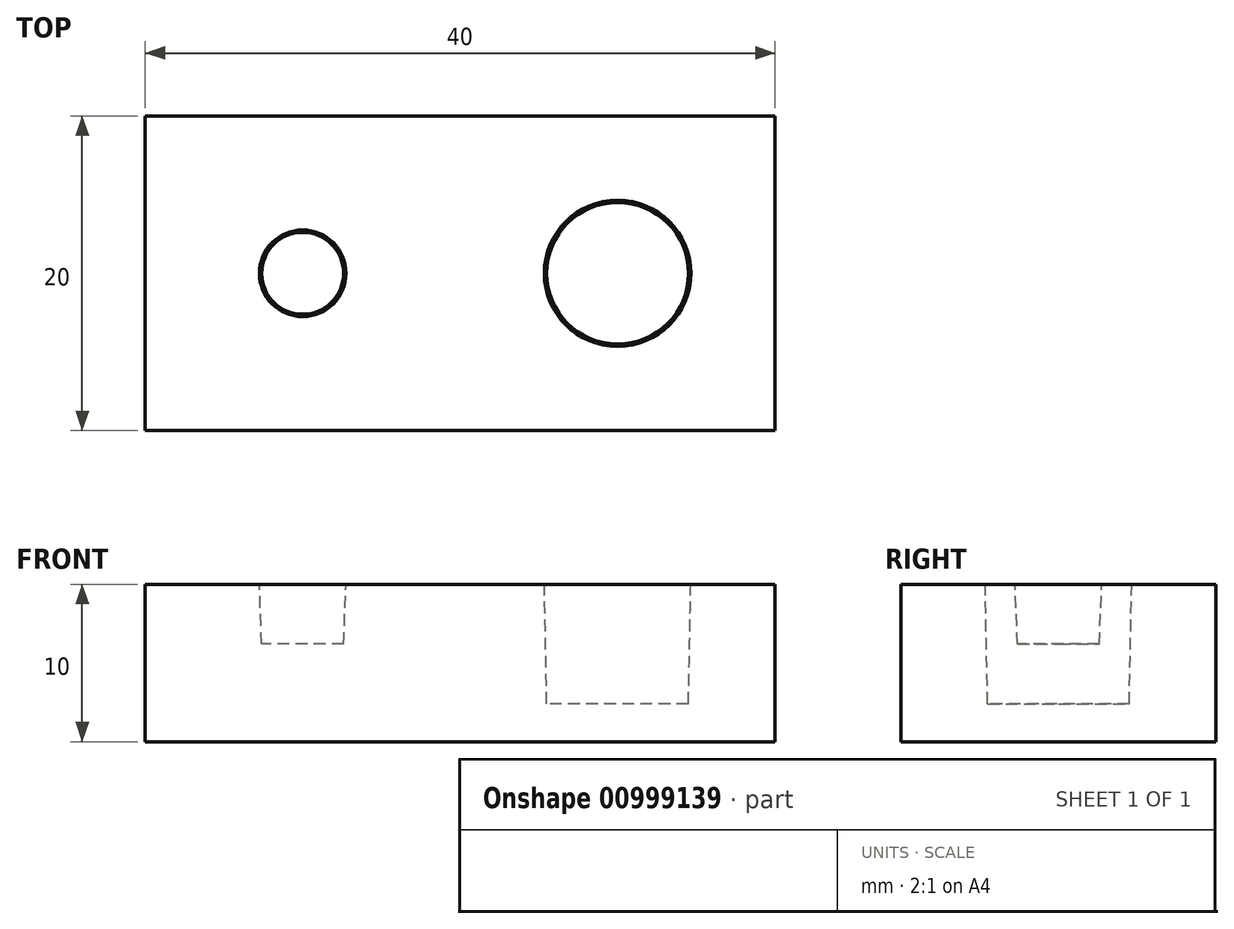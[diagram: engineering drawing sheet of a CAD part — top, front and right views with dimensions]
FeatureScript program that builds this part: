
annotation { "Feature Type Name" : "Feature", "Feature Type Description" : "" }
export const myFeature = defineFeature(function(context is Context, id is Id, definition is map)
    precondition{}
    {
        {
            var Q0;
            Q0=qCreatedBy(makeId("Top.planeOp"),FACE);
            var sketch = newSketch(context, id + "F0", { "sketchPlane" : qUnion([Q0])});
            skLineSegment(sketch, "E0.bottom", {"start": v(-20, 10) * mm, "end": v(20, 10) * mm});
            skLineSegment(sketch, "E0.top", {"start": v(-20, -10) * mm, "end": v(20, -10) * mm});
            skLineSegment(sketch, "E0.left", {"start": v(-20, 10) * mm, "end": v(-20, -10) * mm});
            skLineSegment(sketch, "E0.right", {"start": v(20, 10) * mm, "end": v(20, -10) * mm});
            skPoint(sketch, "E0.middle", {"position": v(0, 0) * mm});
            skSolve(sketch);
        }
        {
            var Q0;
            Q0 = qSketchRegion(id + "F0", true);
            var Q1;
            Q1=makeQuery(id+"F0.imprint","IMPRINT",FACE,{"disambiguationData":[TD([[makeQuery(id+"F0.imprint","IMPRINT",EDGE,{"derivedFrom":sQuery(id+"F0.wireOp",EDGE,"E0.bottom")}),-1.0]])]});
            extrude(context, id + "F1", {"entities" : qUnion([Q0, Q1]), "depth" : 10 * mm, "offsetDistance" : 25 * mm});
        }
        {
            var Q0;
            Q0=makeQuery(id+"F1.opExtrude","CAP_FACE",FACE,{"disambiguationData":[OSD([sQuery(id+"F0.wireOp",EDGE,"E0.bottom"),sQuery(id+"F0.wireOp",EDGE,"E0.top"),sQuery(id+"F0.wireOp",EDGE,"E0.left"),sQuery(id+"F0.wireOp",EDGE,"E0.right")])],"isStart":false});
            var sketch = newSketch(context, id + "F2", { "sketchPlane" : qUnion([Q0])});
            skCircle(sketch, "E1", {"center": v(-10, 0) * mm, "radius": 2.75 * mm});
            skSolve(sketch);
        }
        {
            var Q0;
            Q0=makeQuery(id+"F1.opExtrude","CAP_FACE",FACE,{"disambiguationData":[OSD([sQuery(id+"F0.wireOp",EDGE,"E0.bottom"),sQuery(id+"F0.wireOp",EDGE,"E0.top"),sQuery(id+"F0.wireOp",EDGE,"E0.left"),sQuery(id+"F0.wireOp",EDGE,"E0.right")])],"isStart":false});
            var sketch = newSketch(context, id + "F3", { "sketchPlane" : qUnion([Q0])});
            skSolve(sketch);
        }
        {
            var Q0;
            Q0=makeQuery(id+"F3.imprint","IMPRINT",FACE,{"disambiguationData":[TD([[makeQuery(id+"F3.imprint","IMPRINT",EDGE,{"derivedFrom":makeQuery(id+"F1.opExtrude","CAP_EDGE",EDGE,{"disambiguationData":[OSD([sQuery(id+"F0.wireOp",EDGE,"E0.bottom")])],"isStart":false})}),-1.0]])]});
            cPlane(context, id + "F4", {"entities" : qUnion([Q0]), "cplaneType" : CPlaneType.OFFSET, "offset" : 3.8 * mm, "oppositeDirection" : true, "width" : 150 * mm, "height" : 150 * mm});
        }
        {
            var Q0;
            Q0=qCreatedBy(id+"F4.planeOp",FACE);
            var sketch = newSketch(context, id + "F5", { "sketchPlane" : qUnion([Q0])});
            skCircle(sketch, "E2", {"center": v(-10, 0) * mm, "radius": 2.6 * mm});
            skSolve(sketch);
        }
        {
            var Q1;
            Q1 = qSketchRegion(id + "F2", true);
            var Q2;
            Q2 = qSketchRegion(id + "F5", true);
            loft(context, id + "F6", {"operationType" : NewBodyOperationType.REMOVE, "sheetProfilesArray" : [{ "sheetProfileEntities" : qUnion([Q1]) }, { "sheetProfileEntities" : qUnion([Q2]) }]});
        }
        {
            var Q0;
            Q0=makeQuery(id+"F3.imprint","IMPRINT",FACE,{"disambiguationData":[TD([[makeQuery(id+"F3.imprint","IMPRINT",EDGE,{"derivedFrom":makeQuery(id+"F1.opExtrude","CAP_EDGE",EDGE,{"disambiguationData":[OSD([sQuery(id+"F0.wireOp",EDGE,"E0.bottom")])],"isStart":false})}),-1.0]])]});
            var sketch = newSketch(context, id + "F7", { "sketchPlane" : qUnion([Q0])});
            skCircle(sketch, "E3", {"center": v(10, 0) * mm, "radius": 4.65 * mm});
            skSolve(sketch);
        }
        {
            var Q0;
            Q0=makeQuery(id+"F3.imprint","IMPRINT",FACE,{"disambiguationData":[TD([[makeQuery(id+"F3.imprint","IMPRINT",EDGE,{"derivedFrom":makeQuery(id+"F1.opExtrude","CAP_EDGE",EDGE,{"disambiguationData":[OSD([sQuery(id+"F0.wireOp",EDGE,"E0.bottom")])],"isStart":false})}),-1.0]])]});
            cPlane(context, id + "F8", {"entities" : qUnion([Q0]), "cplaneType" : CPlaneType.OFFSET, "offset" : 7.6 * mm, "oppositeDirection" : true, "width" : 150 * mm, "height" : 150 * mm});
        }
        {
            var Q0;
            Q0=qCreatedBy(id+"F8.planeOp",FACE);
            var sketch = newSketch(context, id + "F9", { "sketchPlane" : qUnion([Q0])});
            skCircle(sketch, "E4", {"center": v(10, 0) * mm, "radius": 4.5 * mm});
            skSolve(sketch);
        }
        {
            var Q1;
            Q1 = qSketchRegion(id + "F7", true);
            var Q2;
            Q2 = qSketchRegion(id + "F9", true);
            loft(context, id + "F10", {"operationType" : NewBodyOperationType.REMOVE, "sheetProfilesArray" : [{ "sheetProfileEntities" : qUnion([Q1]) }, { "sheetProfileEntities" : qUnion([Q2]) }]});
        }
    });
